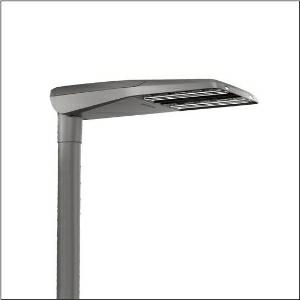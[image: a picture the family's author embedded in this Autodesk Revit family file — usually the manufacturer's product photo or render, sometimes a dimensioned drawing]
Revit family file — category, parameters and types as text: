
# Revit family: streetlight_sl_11_iq_midi___st1_0st0_5_5xc3j51g08me_56cc
name_source: partatom
category: Lighting Fixtures
units: mm (PartAtom-declared; Revit-internal decimal feet)

## family parameters
Cut with Voids When Loaded = No
Host = Face
Light Source = No
Part Type = Normal
Room Calculation Point = No
Round Connector Dimension = Use Diameter
Shared = No

## types (1)
- --- (1 x LED, 17640 lm, 122.6 W, 3000K)
    Apparent Load = 123 VA
    CIE Flux Codes = 35 68 96 100 100
    Color Rendering = 70
    Color Temperature = 3000K
    Default Elevation = 1800 mm
    Description = Streetlight SL 11 iQ midi, mast luminaire, primary light control with 3 zone facetted reflector, of plastic, silver coated, highly specular, primary optical cover: cover, of PMMA, transparent, light distribution: ST1.0ST0.5, light emission: direct distribution, primary light characteristic: asymmetric, installation type: post-top, side-entry, lamps: LED, High Power LED, rated values: 17.640lm | 122,6W | 143,9lm/W (begin service life); end service life: 17.640lm | 130,2W; at 50% lumin. flux: 8.820lm | 56,1W | 157,2lm/W, colour temperature: 3000K, colour rendering: CRI > 70, light colour: 730, light setting 1 begin service life: 100% | 17.640lm | 122,6W | 143,9lm/W | 3.000K, light setting 1 end service life: 130,2W, further light settings possible, control: Street-Remote, Auto-Match, Temp-Guard, Lumen-Switch, Night-Set, Smart-Wire, Light-Fading, Desk-Remote (wireless, voltage-free reading and setting of iQ features in the workshop via application-optimized NFC function/RFID function), optimised constant luminous flux control (CLO 2.0), pre-setting: linear dimming characteristic, with cable H07RN-F 5x 1.5mm², mains connection: 230..240V, AC, 50/60Hz, connection cable pre-assembled, cable length: 12,5m, luminaire housing, of diecast aluminium, powder-coated, Siteco® metallic grey (DB 702S), please order mast flange separately, inclination adjustable without tools: 0°, 5°, 10°, 15° (post-top) | 0°, -5°, -10°, -15° (side-entry), sealing non-destructively replaceable, multi-level sealing system, length: 780mm, width: 376mm, height: 118mm, mast flange for spigot size: 42mm (side-entry): 5XC10008XM4, 60/48mm (side-entry/post-top): 5XC10108XM2, 76/60mm (side-entry/post-top): 5XC10108XM1, equipment: Power, protection rating (complete): IP66, insulation class (complete): insulation class II (safety insulation), certification: CE, ENEC, ENEC+, VDE, impact resistance: IK10, permissible operating ambient temperature for outdoor applications: -25..+50°C, standard-compliant lighting for roads and squares, Environmental Product Declaration (EPD) tested and certified by an independent institute, packaging unit: 1 piece

Light Distribution: ST1.0ST0.5
    Height = 118 mm
    Lamp = 1 x LED
    Lamp Light Flux = 17640 lm
    Lamp Power = 122.6 W
    Lamp count = 1
    Length = 780 mm
    Luminous efficacy = 144 lm/W
    Manufacturer = Siteco
    ModVariant = No
    Model = 5XC3J51G08ME
    Number of Poles = 1
    OnlyDefault = Yes
    Power Factor = 1
    Product Name = Streetlight SL 11 iQ midi | ST1.0ST0.5
    Product group = mast luminaire | pylon top
    ProductGroupID = 6100
    Protection Class = Protection class II
    Protection Degree = IP 66
    RLX_Detail_Level = 1
    RLX_Emergency_Light_Flux = 0 lm
    RLX_Emergency_Type = 0
    RLX_Emergency_Type_DB = No
    RlxData = <blob elided: 71029 chars, md5=0c2683ab>
    Socket = socket
    Standby Power = 0 W
    System Light Flux = 17640 lm
    System Power = 123 W
    Type Comments = factory setting: luminous flux: 100 % | dim-lin: 254 | 552 mA
    Type Image = l_1005960.jpg
    URL = http://relux.com
    VarID = @adj_006659
    Voltage = 0 V
    Weight = 0.00 kg
    Width = 376 mm

## geometry (parser evidence)
native form markers: Blend x4, Sweep x9
no freeform markers — native parametric forms only
